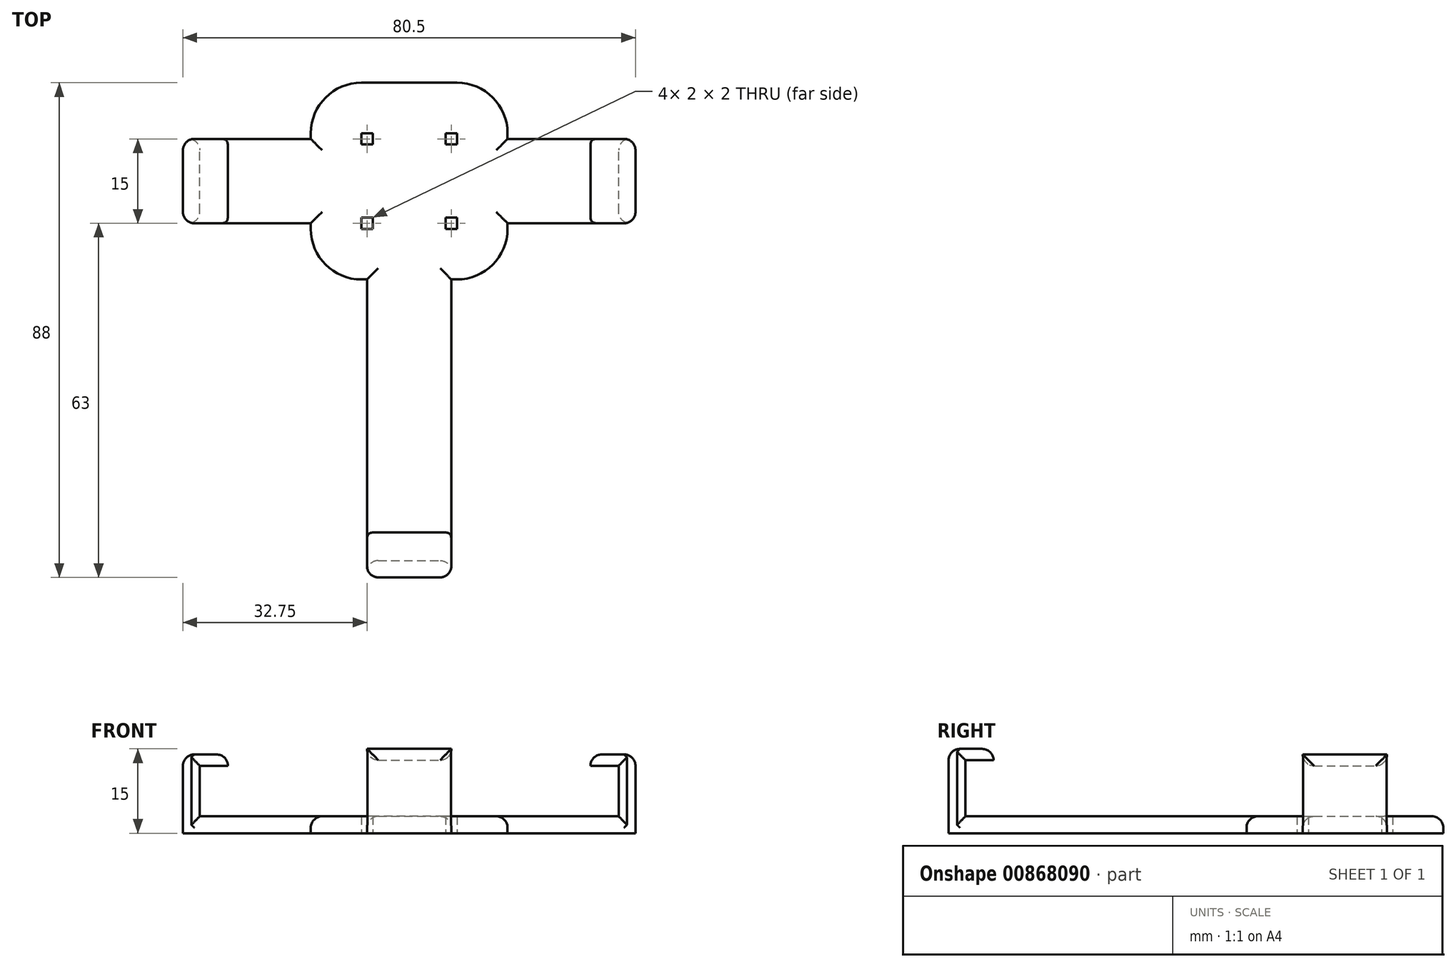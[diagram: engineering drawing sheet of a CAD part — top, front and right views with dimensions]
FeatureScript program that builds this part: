
annotation { "Feature Type Name" : "Feature", "Feature Type Description" : "" }
export const myFeature = defineFeature(function(context is Context, id is Id, definition is map)
    precondition{}
    {
        {
            var Q0;
            Q0=qCreatedBy(makeId("Top.planeOp"),FACE);
            var sketch = newSketch(context, id + "F0", { "sketchPlane" : qUnion([Q0])});
            skLineSegment(sketch, "E0.bottom", {"start": v(17.5, -17.5) * mm, "end": v(-17.5, -17.5) * mm});
            skLineSegment(sketch, "E0.top", {"start": v(17.5, 17.5) * mm, "end": v(-17.5, 17.5) * mm});
            skLineSegment(sketch, "E0.left", {"start": v(17.5, -17.5) * mm, "end": v(17.5, 17.5) * mm});
            skLineSegment(sketch, "E0.right", {"start": v(-17.5, -17.5) * mm, "end": v(-17.5, 17.5) * mm});
            skPoint(sketch, "E0.middle", {"position": v(0, 0) * mm});
            skLineSegment(sketch, "E1.bottom", {"start": v(37.25, -7.5) * mm, "end": v(-37.25, -7.5) * mm});
            skLineSegment(sketch, "E1.top", {"start": v(37.25, 7.5) * mm, "end": v(-37.25, 7.5) * mm});
            skLineSegment(sketch, "E1.left", {"start": v(37.25, -7.5) * mm, "end": v(37.25, 7.5) * mm});
            skLineSegment(sketch, "E1.right", {"start": v(-37.25, -7.5) * mm, "end": v(-37.25, 7.5) * mm});
            skLineSegment(sketch, "E2.bottom", {"start": v(-37.25, 7.5) * mm, "end": v(-40.25, 7.5) * mm});
            skLineSegment(sketch, "E2.top", {"start": v(-37.25, -7.5) * mm, "end": v(-40.25, -7.5) * mm});
            skLineSegment(sketch, "E2.left", {"start": v(-37.25, 7.5) * mm, "end": v(-37.25, -7.5) * mm});
            skLineSegment(sketch, "E2.right", {"start": v(-40.25, 7.5) * mm, "end": v(-40.25, -7.5) * mm});
            skLineSegment(sketch, "E3.bottom", {"start": v(37.25, 7.5) * mm, "end": v(40.25, 7.5) * mm});
            skLineSegment(sketch, "E3.top", {"start": v(37.25, -7.5) * mm, "end": v(40.25, -7.5) * mm});
            skLineSegment(sketch, "E3.left", {"start": v(37.25, 7.5) * mm, "end": v(37.25, -7.5) * mm});
            skLineSegment(sketch, "E3.right", {"start": v(40.25, 7.5) * mm, "end": v(40.25, -7.5) * mm});
            skLineSegment(sketch, "E4.bottom", {"start": v(-7.5, -7.5) * mm, "end": v(7.5, -7.5) * mm});
            skLineSegment(sketch, "E4.top", {"start": v(-7.5, -67.5) * mm, "end": v(7.5, -67.5) * mm});
            skLineSegment(sketch, "E4.left", {"start": v(-7.5, -7.5) * mm, "end": v(-7.5, -67.5) * mm});
            skLineSegment(sketch, "E4.right", {"start": v(7.5, -7.5) * mm, "end": v(7.5, -67.5) * mm});
            skLineSegment(sketch, "E5.top", {"start": v(-7.5, -70.5) * mm, "end": v(7.5, -70.5) * mm});
            skLineSegment(sketch, "E5.left", {"start": v(-7.5, -67.5) * mm, "end": v(-7.5, -70.5) * mm});
            skLineSegment(sketch, "E5.right", {"start": v(7.5, -67.5) * mm, "end": v(7.5, -70.5) * mm});
            skLineSegment(sketch, "E6", {"start": v(17.5, 17.5) * mm, "end": v(-17.5, -17.5) * mm, "construction": true});
            skLineSegment(sketch, "E7", {"start": v(-17.5, 17.5) * mm, "end": v(17.5, -17.5) * mm, "construction": true});
            skLineSegment(sketch, "E8", {"start": v(0, 17.5) * mm, "end": v(0, -17.5) * mm, "construction": true});
            skLineSegment(sketch, "E9", {"start": v(17.5, 0) * mm, "end": v(-17.5, 0) * mm, "construction": true});
            skLineSegment(sketch, "E10.bottom", {"start": v(6.5, 8.5) * mm, "end": v(8.5, 8.5) * mm});
            skLineSegment(sketch, "E10.top", {"start": v(6.5, 6.5) * mm, "end": v(8.5, 6.5) * mm});
            skLineSegment(sketch, "E10.left", {"start": v(6.5, 8.5) * mm, "end": v(6.5, 6.5) * mm});
            skLineSegment(sketch, "E10.right", {"start": v(8.5, 8.5) * mm, "end": v(8.5, 6.5) * mm});
            skPoint(sketch, "E10.middle", {"position": v(7.5, 7.5) * mm});
            skPoint(sketch, "E11.middle", {"position": v(-7.5, 7.5) * mm});
            skLineSegment(sketch, "E12.bottom", {"start": v(-8.5, -6.5) * mm, "end": v(-6.5, -6.5) * mm});
            skLineSegment(sketch, "E12.top", {"start": v(-8.5, -8.5) * mm, "end": v(-6.5, -8.5) * mm});
            skLineSegment(sketch, "E12.left", {"start": v(-8.5, -6.5) * mm, "end": v(-8.5, -8.5) * mm});
            skLineSegment(sketch, "E12.right", {"start": v(-6.5, -6.5) * mm, "end": v(-6.5, -8.5) * mm});
            skPoint(sketch, "E12.middle", {"position": v(-7.5, -7.5) * mm});
            skLineSegment(sketch, "E13.bottom", {"start": v(6.5, -6.5) * mm, "end": v(8.5, -6.5) * mm});
            skLineSegment(sketch, "E13.top", {"start": v(6.5, -8.5) * mm, "end": v(8.5, -8.5) * mm});
            skLineSegment(sketch, "E13.left", {"start": v(6.5, -6.5) * mm, "end": v(6.5, -8.5) * mm});
            skLineSegment(sketch, "E13.right", {"start": v(8.5, -6.5) * mm, "end": v(8.5, -8.5) * mm});
            skPoint(sketch, "E13.middle", {"position": v(7.5, -7.5) * mm});
            skLineSegment(sketch, "E14.MirrorCS", {"start": v(-6.5, 8.5) * mm, "end": v(-6.5, 6.5) * mm});
            skLineSegment(sketch, "E15.MirrorCS", {"start": v(-6.5, 8.5) * mm, "end": v(-8.5, 8.5) * mm});
            skLineSegment(sketch, "E16.MirrorCS", {"start": v(-8.5, 8.5) * mm, "end": v(-8.5, 6.5) * mm});
            skLineSegment(sketch, "E17.MirrorCS", {"start": v(-6.5, 6.5) * mm, "end": v(-8.5, 6.5) * mm});
            skSolve(sketch);
        }
        {
            var Q0;
            {var subQ1=sQuery(id+"F0.wireOp",EDGE,"E12.bottom");var subQ7=sQuery(id+"F0.wireOp",EDGE,"E13.bottom");Q0=qUnion([makeQuery(id+"F0.imprint","IMPRINT",FACE,{"disambiguationData":[TD([[makeQuery(id+"F0.imprint","IMPRINT",EDGE,{"derivedFrom":subQ7}),-1.0]])]}),makeQuery(id+"F0.imprint","IMPRINT",FACE,{"disambiguationData":[TD([[makeQuery(id+"F0.imprint","IMPRINT",EDGE,{"derivedFrom":subQ1}),-1.0]])]})]);}
            var Q1;
            {var subQ15=sQuery(id+"F0.wireOp",EDGE,"E0.top");Q1=makeQuery(id+"F0.imprint","IMPRINT",FACE,{"disambiguationData":[TD([[makeQuery(id+"F0.imprint","IMPRINT",EDGE,{"derivedFrom":subQ15}),1.0]])]});}
            var Q2;
            {var subQ5=sQuery(id+"F0.wireOp",EDGE,"E1.right");Q2=makeQuery(id+"F0.imprint","IMPRINT",FACE,{"disambiguationData":[TD([[makeQuery(id+"F0.imprint","IMPRINT",EDGE,{"derivedFrom":subQ5}),-1.0]])]});}
            var Q3;
            {var subQ1=sQuery(id+"F0.wireOp",EDGE,"E0.bottom");var subQ6=sQuery(id+"F0.wireOp",EDGE,"E0.right");var subQ10=makeQuery(id+"F0.imprint","INTERSECT",VERTEX,{"derivedFrom":[subQ1,subQ6]});Q3=makeQuery(id+"F0.imprint","IMPRINT",FACE,{"disambiguationData":[TD([[makeQuery(id+"F0.imprint","IMPRINT",EDGE,{"disambiguationData":[TD([[subQ10,1.0]])],"derivedFrom":subQ1}),-1.0]])]});}
            var Q4;
            {var subQ0=sQuery(id+"F0.wireOp",EDGE,"E4.left");var subQ1=sQuery(id+"F0.wireOp",EDGE,"E1.bottom");var subQ2=makeQuery(id+"F0.imprint","INTERSECT",VERTEX,{"derivedFrom":[subQ1,subQ0]});var subQ8=sQuery(id+"F0.wireOp",EDGE,"E13.left");var subQ9=makeQuery(id+"F0.imprint","INTERSECT",VERTEX,{"derivedFrom":[subQ1,subQ8]});Q4=qUnion([makeQuery(id+"F0.imprint","IMPRINT",FACE,{"disambiguationData":[TD([[makeQuery(id+"F0.imprint","IMPRINT",EDGE,{"disambiguationData":[TD([[subQ9,1.0]])],"derivedFrom":subQ1}),1.0]])]}),makeQuery(id+"F0.imprint","IMPRINT",FACE,{"disambiguationData":[TD([[makeQuery(id+"F0.imprint","IMPRINT",EDGE,{"disambiguationData":[TD([[subQ2,1.0]])],"derivedFrom":subQ1}),1.0]])]})]);}
            var Q5;
            {var subQ0=sQuery(id+"F0.wireOp",EDGE,"E4.right");var subQ1=sQuery(id+"F0.wireOp",EDGE,"E0.bottom");var subQ2=makeQuery(id+"F0.imprint","INTERSECT",VERTEX,{"derivedFrom":[subQ1,subQ0]});Q5=makeQuery(id+"F0.imprint","IMPRINT",FACE,{"disambiguationData":[TD([[makeQuery(id+"F0.imprint","IMPRINT",EDGE,{"disambiguationData":[TD([[subQ2,1.0]])],"derivedFrom":subQ1}),-1.0]])]});}
            var Q6;
            {var subQ5=sQuery(id+"F0.wireOp",EDGE,"E1.left");Q6=makeQuery(id+"F0.imprint","IMPRINT",FACE,{"disambiguationData":[TD([[makeQuery(id+"F0.imprint","IMPRINT",EDGE,{"derivedFrom":subQ5}),1.0]])]});}
            var Q7;
            {var subQ5=sQuery(id+"F0.wireOp",EDGE,"E4.top");Q7=makeQuery(id+"F0.imprint","IMPRINT",FACE,{"disambiguationData":[TD([[makeQuery(id+"F0.imprint","IMPRINT",EDGE,{"derivedFrom":subQ5}),1.0]])]});}
            var Q8;
            {var subQ5=sQuery(id+"F0.wireOp",EDGE,"E10.top");Q8=makeQuery(id+"F0.imprint","IMPRINT",FACE,{"disambiguationData":[TD([[makeQuery(id+"F0.imprint","IMPRINT",EDGE,{"derivedFrom":subQ5}),-1.0]])]});}
            var Q9;
            {var subQ0=sQuery(id+"F0.wireOp",EDGE,"E4.right");var subQ1=sQuery(id+"F0.wireOp",EDGE,"E0.bottom");var subQ2=makeQuery(id+"F0.imprint","INTERSECT",VERTEX,{"derivedFrom":[subQ1,subQ0]});Q9=makeQuery(id+"F0.imprint","IMPRINT",FACE,{"disambiguationData":[TD([[makeQuery(id+"F0.imprint","IMPRINT",EDGE,{"disambiguationData":[TD([[subQ2,-1.0]])],"derivedFrom":subQ1}),-1.0]])]});}
            extrude(context, id + "F1", {"entities" : qUnion([Q0, Q1, Q2, Q3, Q4, Q5, Q6, Q7, Q8, Q9]), "depth" : 3 * mm, "offsetDistance" : 25 * mm});
        }
        {
            var Q0;
            Q0=makeQuery(id+"F0.imprint","IMPRINT",FACE,{"disambiguationData":[TD([[makeQuery(id+"F0.imprint","IMPRINT",EDGE,{"derivedFrom":sQuery(id+"F0.wireOp",EDGE,"E1.right")}),1.0]])]});
            var Q1;
            Q1=makeQuery(id+"F0.imprint","IMPRINT",FACE,{"disambiguationData":[TD([[makeQuery(id+"F0.imprint","IMPRINT",EDGE,{"derivedFrom":sQuery(id+"F0.wireOp",EDGE,"E1.left")}),-1.0]])]});
            extrude(context, id + "F2", {"entities" : qUnion([Q0, Q1]), "operationType" : NewBodyOperationType.ADD, "depth" : 14 * mm, "offsetDistance" : 25 * mm});
        }
        {
            var Q0;
            Q0=makeQuery(id+"F0.imprint","IMPRINT",FACE,{"disambiguationData":[TD([[makeQuery(id+"F0.imprint","IMPRINT",EDGE,{"derivedFrom":sQuery(id+"F0.wireOp",EDGE,"E4.top")}),-1.0]])]});
            extrude(context, id + "F3", {"entities" : qUnion([Q0]), "operationType" : NewBodyOperationType.ADD, "depth" : 15 * mm, "offsetDistance" : 25 * mm});
        }
        {
            var Q0;
            Q0=makeQuery(id+"F3.opExtrude","SWEPT_FACE",FACE,{"disambiguationData":[OSD([sQuery(id+"F0.wireOp",EDGE,"E4.top")])]});
            var sketch = newSketch(context, id + "F4", { "sketchPlane" : qUnion([Q0])});
            skLineSegment(sketch, "E18.bottom", {"start": v(7.5, 15) * mm, "end": v(-7.5, 15) * mm});
            skLineSegment(sketch, "E18.top", {"start": v(7.5, 13) * mm, "end": v(-7.5, 13) * mm});
            skLineSegment(sketch, "E18.left", {"start": v(7.5, 15) * mm, "end": v(7.5, 13) * mm});
            skLineSegment(sketch, "E18.right", {"start": v(-7.5, 15) * mm, "end": v(-7.5, 13) * mm});
            skSolve(sketch);
        }
        {
            var Q0;
            Q0 = qSketchRegion(id + "F4", true);
            extrude(context, id + "F5", {"entities" : qUnion([Q0]), "operationType" : NewBodyOperationType.ADD, "depth" : 5 * mm, "offsetDistance" : 25 * mm});
        }
        {
            var Q0;
            Q0=makeQuery(id+"F2.opExtrude","SWEPT_FACE",FACE,{"disambiguationData":[OSD([sQuery(id+"F0.wireOp",EDGE,"E1.right")])]});
            var sketch = newSketch(context, id + "F6", { "sketchPlane" : qUnion([Q0])});
            skLineSegment(sketch, "E19.bottom", {"start": v(7.5, 14) * mm, "end": v(-7.5, 14) * mm});
            skLineSegment(sketch, "E19.top", {"start": v(7.5, 12) * mm, "end": v(-7.5, 12) * mm});
            skLineSegment(sketch, "E19.left", {"start": v(7.5, 14) * mm, "end": v(7.5, 12) * mm});
            skLineSegment(sketch, "E19.right", {"start": v(-7.5, 14) * mm, "end": v(-7.5, 12) * mm});
            skSolve(sketch);
        }
        {
            var Q0;
            Q0 = qSketchRegion(id + "F6", true);
            extrude(context, id + "F7", {"entities" : qUnion([Q0]), "operationType" : NewBodyOperationType.ADD, "depth" : 5 * mm, "offsetDistance" : 25 * mm});
        }
        {
            var Q0;
            Q0=makeQuery(id+"F2.opExtrude","SWEPT_FACE",FACE,{"disambiguationData":[OSD([sQuery(id+"F0.wireOp",EDGE,"E1.left")])]});
            var sketch = newSketch(context, id + "F8", { "sketchPlane" : qUnion([Q0])});
            skLineSegment(sketch, "E20.bottom", {"start": v(7.5, 14) * mm, "end": v(-7.5, 14) * mm});
            skLineSegment(sketch, "E20.top", {"start": v(7.5, 12) * mm, "end": v(-7.5, 12) * mm});
            skLineSegment(sketch, "E20.left", {"start": v(7.5, 14) * mm, "end": v(7.5, 12) * mm});
            skLineSegment(sketch, "E20.right", {"start": v(-7.5, 14) * mm, "end": v(-7.5, 12) * mm});
            skSolve(sketch);
        }
        {
            var Q0;
            Q0 = qSketchRegion(id + "F8", true);
            extrude(context, id + "F9", {"entities" : qUnion([Q0]), "operationType" : NewBodyOperationType.ADD, "depth" : 5 * mm, "offsetDistance" : 25 * mm});
        }
        {
            var Q0;
            {var subQ0=sQuery(id+"F0.wireOp",EDGE,"E13.left");var subQ1=sQuery(id+"F0.wireOp",EDGE,"E1.bottom");var subQ2=makeQuery(id+"F0.imprint","INTERSECT",VERTEX,{"derivedFrom":[subQ1,subQ0]});Q0=makeQuery(id+"F0.imprint","IMPRINT",FACE,{"disambiguationData":[TD([[makeQuery(id+"F0.imprint","IMPRINT",EDGE,{"disambiguationData":[TD([[subQ2,1.0]])],"derivedFrom":subQ1}),1.0]])]});}
            var Q1;
            {var subQ0=sQuery(id+"F0.wireOp",EDGE,"E4.right");var subQ1=sQuery(id+"F0.wireOp",EDGE,"E1.bottom");var subQ2=makeQuery(id+"F0.imprint","INTERSECT",VERTEX,{"derivedFrom":[subQ1,subQ0]});Q1=makeQuery(id+"F0.imprint","IMPRINT",FACE,{"disambiguationData":[TD([[makeQuery(id+"F0.imprint","IMPRINT",EDGE,{"disambiguationData":[TD([[subQ2,1.0]])],"derivedFrom":subQ1}),1.0]])]});}
            var Q2;
            {var subQ0=sQuery(id+"F0.wireOp",EDGE,"E13.bottom");Q2=makeQuery(id+"F0.imprint","IMPRINT",FACE,{"disambiguationData":[TD([[makeQuery(id+"F0.imprint","IMPRINT",EDGE,{"derivedFrom":subQ0}),-1.0]])]});}
            var Q3;
            {var subQ5=sQuery(id+"F0.wireOp",EDGE,"E10.bottom");Q3=makeQuery(id+"F0.imprint","IMPRINT",FACE,{"disambiguationData":[TD([[makeQuery(id+"F0.imprint","IMPRINT",EDGE,{"derivedFrom":subQ5}),-1.0]])]});}
            var Q4;
            {var subQ5=sQuery(id+"F0.wireOp",EDGE,"E10.top");Q4=makeQuery(id+"F0.imprint","IMPRINT",FACE,{"disambiguationData":[TD([[makeQuery(id+"F0.imprint","IMPRINT",EDGE,{"derivedFrom":subQ5}),1.0]])]});}
            var Q5;
            {var subQ5=sQuery(id+"F0.wireOp",EDGE,"E17.MirrorCS");Q5=makeQuery(id+"F0.imprint","IMPRINT",FACE,{"disambiguationData":[TD([[makeQuery(id+"F0.imprint","IMPRINT",EDGE,{"derivedFrom":subQ5}),-1.0]])]});}
            var Q6;
            {var subQ5=sQuery(id+"F0.wireOp",EDGE,"E15.MirrorCS");Q6=makeQuery(id+"F0.imprint","IMPRINT",FACE,{"disambiguationData":[TD([[makeQuery(id+"F0.imprint","IMPRINT",EDGE,{"derivedFrom":subQ5}),1.0]])]});}
            var Q7;
            {var subQ1=sQuery(id+"F0.wireOp",EDGE,"E12.bottom");Q7=makeQuery(id+"F0.imprint","IMPRINT",FACE,{"disambiguationData":[TD([[makeQuery(id+"F0.imprint","IMPRINT",EDGE,{"derivedFrom":subQ1}),-1.0]])]});}
            var Q8;
            {var subQ0=sQuery(id+"F0.wireOp",EDGE,"E4.left");var subQ1=sQuery(id+"F0.wireOp",EDGE,"E1.bottom");var subQ2=makeQuery(id+"F0.imprint","INTERSECT",VERTEX,{"derivedFrom":[subQ1,subQ0]});Q8=makeQuery(id+"F0.imprint","IMPRINT",FACE,{"disambiguationData":[TD([[makeQuery(id+"F0.imprint","IMPRINT",EDGE,{"disambiguationData":[TD([[subQ2,-1.0]])],"derivedFrom":subQ1}),1.0]])]});}
            var Q9;
            {var subQ0=sQuery(id+"F0.wireOp",EDGE,"E4.left");var subQ1=sQuery(id+"F0.wireOp",EDGE,"E1.bottom");var subQ2=makeQuery(id+"F0.imprint","INTERSECT",VERTEX,{"derivedFrom":[subQ1,subQ0]});Q9=makeQuery(id+"F0.imprint","IMPRINT",FACE,{"disambiguationData":[TD([[makeQuery(id+"F0.imprint","IMPRINT",EDGE,{"disambiguationData":[TD([[subQ2,1.0]])],"derivedFrom":subQ1}),1.0]])]});}
            extrude(context, id + "F10", {"entities" : qUnion([Q0, Q1, Q2, Q3, Q4, Q5, Q6, Q7, Q8, Q9]), "operationType" : NewBodyOperationType.REMOVE, "depth" : 25 * mm, "offsetDistance" : 25 * mm});
        }
        {
            var Q0;
            Q0=makeQuery(id+"F2.opExtrude","CAP_EDGE",EDGE,{"disambiguationData":[OSD([sQuery(id+"F0.wireOp",EDGE,"E2.right")])],"isStart":false});
            var Q1;
            Q1=makeQuery(id+"F2.opExtrude","CAP_EDGE",EDGE,{"disambiguationData":[OSD([sQuery(id+"F0.wireOp",EDGE,"E3.right")])],"isStart":false});
            var Q2;
            Q2=makeQuery(id+"F3.opExtrude","CAP_EDGE",EDGE,{"disambiguationData":[OSD([sQuery(id+"F0.wireOp",EDGE,"E5.top")])],"isStart":false});
            var Q3;
            Q3=makeQuery(id+"F2.opExtrude","SWEPT_EDGE",EDGE,{"disambiguationData":[OSD([sQuery(id+"F0.wireOp",EDGE,"E2.top"),sQuery(id+"F0.wireOp",EDGE,"E2.right")])]});
            var Q4;
            Q4=makeQuery(id+"F2.opExtrude","SWEPT_EDGE",EDGE,{"disambiguationData":[OSD([sQuery(id+"F0.wireOp",EDGE,"E2.bottom"),sQuery(id+"F0.wireOp",EDGE,"E2.right")])]});
            var Q5;
            Q5=makeQuery(id+"F2.opExtrude","SWEPT_EDGE",EDGE,{"disambiguationData":[OSD([sQuery(id+"F0.wireOp",EDGE,"E3.top"),sQuery(id+"F0.wireOp",EDGE,"E3.right")])]});
            var Q6;
            Q6=makeQuery(id+"F2.opExtrude","SWEPT_EDGE",EDGE,{"disambiguationData":[OSD([sQuery(id+"F0.wireOp",EDGE,"E3.bottom"),sQuery(id+"F0.wireOp",EDGE,"E3.right")])]});
            var Q7;
            Q7=makeQuery(id+"F3.opExtrude","SWEPT_EDGE",EDGE,{"disambiguationData":[OSD([sQuery(id+"F0.wireOp",EDGE,"E5.top"),sQuery(id+"F0.wireOp",EDGE,"E5.left")])]});
            var Q8;
            Q8=makeQuery(id+"F3.opExtrude","SWEPT_EDGE",EDGE,{"disambiguationData":[OSD([sQuery(id+"F0.wireOp",EDGE,"E5.top"),sQuery(id+"F0.wireOp",EDGE,"E5.right")])]});
            var Q9;
            Q9=makeQuery(id+"F9.opExtrude","CAP_EDGE",EDGE,{"disambiguationData":[OSD([sQuery(id+"F8.wireOp",EDGE,"E20.bottom")])],"isStart":false});
            var Q10;
            Q10=makeQuery(id+"F7.opExtrude","CAP_EDGE",EDGE,{"disambiguationData":[OSD([sQuery(id+"F6.wireOp",EDGE,"E19.bottom")])],"isStart":false});
            var Q11;
            Q11=makeQuery(id+"F5.opExtrude","CAP_EDGE",EDGE,{"disambiguationData":[OSD([sQuery(id+"F4.wireOp",EDGE,"E18.bottom")])],"isStart":false});
            var Q12;
            {var subQ0=sQuery(id+"F0.wireOp",EDGE,"E4.left");Q12=makeQuery(id+"F1.opExtrude","CAP_EDGE",EDGE,{"disambiguationData":[OSD([subQ0]),TDD([makeQuery(id+"F0.imprint","IMPRINT",EDGE,{"disambiguationData":[TD([[makeQuery(id+"F0.imprint","INTERSECT",VERTEX,{"derivedFrom":[sQuery(id+"F0.wireOp",EDGE,"E0.bottom"),subQ0]}),-1.0]])],"derivedFrom":subQ0})])],"isStart":false});}
            var Q13;
            {var subQ0=sQuery(id+"F0.wireOp",EDGE,"E4.right");Q13=makeQuery(id+"F1.opExtrude","CAP_EDGE",EDGE,{"disambiguationData":[OSD([subQ0]),TDD([makeQuery(id+"F0.imprint","IMPRINT",EDGE,{"disambiguationData":[TD([[makeQuery(id+"F0.imprint","INTERSECT",VERTEX,{"derivedFrom":[sQuery(id+"F0.wireOp",EDGE,"E0.bottom"),subQ0]}),-1.0]])],"derivedFrom":subQ0})])],"isStart":false});}
            var Q14;
            {var subQ0=sQuery(id+"F0.wireOp",EDGE,"E0.bottom");Q14=makeQuery(id+"F1.opExtrude","CAP_EDGE",EDGE,{"disambiguationData":[OSD([subQ0]),TDD([makeQuery(id+"F0.imprint","IMPRINT",EDGE,{"disambiguationData":[TD([[makeQuery(id+"F0.imprint","INTERSECT",VERTEX,{"derivedFrom":[subQ0,sQuery(id+"F0.wireOp",EDGE,"E4.right")]}),1.0]])],"derivedFrom":subQ0})])],"isStart":false});}
            var Q15;
            {var subQ0=sQuery(id+"F0.wireOp",EDGE,"E0.bottom");Q15=makeQuery(id+"F1.opExtrude","CAP_EDGE",EDGE,{"disambiguationData":[OSD([subQ0]),TDD([makeQuery(id+"F0.imprint","IMPRINT",EDGE,{"disambiguationData":[TD([[makeQuery(id+"F0.imprint","INTERSECT",VERTEX,{"derivedFrom":[subQ0,sQuery(id+"F0.wireOp",EDGE,"E0.right")]}),1.0]])],"derivedFrom":subQ0})])],"isStart":false});}
            var Q16;
            {var subQ0=sQuery(id+"F0.wireOp",EDGE,"E0.right");Q16=makeQuery(id+"F1.opExtrude","CAP_EDGE",EDGE,{"disambiguationData":[OSD([subQ0]),TDD([makeQuery(id+"F0.imprint","IMPRINT",EDGE,{"disambiguationData":[TD([[makeQuery(id+"F0.imprint","INTERSECT",VERTEX,{"derivedFrom":[sQuery(id+"F0.wireOp",EDGE,"E0.bottom"),subQ0]}),-1.0]])],"derivedFrom":subQ0})])],"isStart":false});}
            var Q17;
            {var subQ0=sQuery(id+"F0.wireOp",EDGE,"E0.right");Q17=makeQuery(id+"F1.opExtrude","CAP_EDGE",EDGE,{"disambiguationData":[OSD([subQ0]),TDD([makeQuery(id+"F0.imprint","IMPRINT",EDGE,{"disambiguationData":[TD([[makeQuery(id+"F0.imprint","INTERSECT",VERTEX,{"derivedFrom":[sQuery(id+"F0.wireOp",EDGE,"E0.top"),subQ0]}),1.0]])],"derivedFrom":subQ0})])],"isStart":false});}
            var Q18;
            Q18=makeQuery(id+"F1.opExtrude","CAP_EDGE",EDGE,{"disambiguationData":[OSD([sQuery(id+"F0.wireOp",EDGE,"E0.top")])],"isStart":false});
            var Q19;
            {var subQ0=sQuery(id+"F0.wireOp",EDGE,"E0.left");Q19=makeQuery(id+"F1.opExtrude","CAP_EDGE",EDGE,{"disambiguationData":[OSD([subQ0]),TDD([makeQuery(id+"F0.imprint","IMPRINT",EDGE,{"disambiguationData":[TD([[makeQuery(id+"F0.imprint","INTERSECT",VERTEX,{"derivedFrom":[sQuery(id+"F0.wireOp",EDGE,"E0.top"),subQ0]}),1.0]])],"derivedFrom":subQ0})])],"isStart":false});}
            var Q20;
            {var subQ0=sQuery(id+"F0.wireOp",EDGE,"E0.left");Q20=makeQuery(id+"F1.opExtrude","CAP_EDGE",EDGE,{"disambiguationData":[OSD([subQ0]),TDD([makeQuery(id+"F0.imprint","IMPRINT",EDGE,{"disambiguationData":[TD([[makeQuery(id+"F0.imprint","INTERSECT",VERTEX,{"derivedFrom":[subQ0,sQuery(id+"F0.wireOp",EDGE,"E1.bottom")]}),1.0]])],"derivedFrom":subQ0})])],"isStart":false});}
            var Q21;
            {var subQ0=sQuery(id+"F0.wireOp",EDGE,"E1.bottom");Q21=makeQuery(id+"F1.opExtrude","CAP_EDGE",EDGE,{"disambiguationData":[OSD([subQ0]),TDD([makeQuery(id+"F0.imprint","IMPRINT",EDGE,{"disambiguationData":[TD([[makeQuery(id+"F0.imprint","INTERSECT",VERTEX,{"derivedFrom":[sQuery(id+"F0.wireOp",EDGE,"E0.right"),subQ0]}),-1.0]])],"derivedFrom":subQ0})])],"isStart":false});}
            var Q22;
            {var subQ0=sQuery(id+"F0.wireOp",EDGE,"E1.top");Q22=makeQuery(id+"F1.opExtrude","CAP_EDGE",EDGE,{"disambiguationData":[OSD([subQ0]),TDD([makeQuery(id+"F0.imprint","IMPRINT",EDGE,{"disambiguationData":[TD([[makeQuery(id+"F0.imprint","INTERSECT",VERTEX,{"derivedFrom":[sQuery(id+"F0.wireOp",EDGE,"E0.right"),subQ0]}),-1.0]])],"derivedFrom":subQ0})])],"isStart":false});}
            var Q23;
            {var subQ0=sQuery(id+"F0.wireOp",EDGE,"E1.top");Q23=makeQuery(id+"F1.opExtrude","CAP_EDGE",EDGE,{"disambiguationData":[OSD([subQ0]),TDD([makeQuery(id+"F0.imprint","IMPRINT",EDGE,{"disambiguationData":[TD([[makeQuery(id+"F0.imprint","INTERSECT",VERTEX,{"derivedFrom":[sQuery(id+"F0.wireOp",EDGE,"E0.left"),subQ0]}),1.0]])],"derivedFrom":subQ0})])],"isStart":false});}
            var Q24;
            {var subQ0=sQuery(id+"F0.wireOp",EDGE,"E1.bottom");Q24=makeQuery(id+"F1.opExtrude","CAP_EDGE",EDGE,{"disambiguationData":[OSD([subQ0]),TDD([makeQuery(id+"F0.imprint","IMPRINT",EDGE,{"disambiguationData":[TD([[makeQuery(id+"F0.imprint","INTERSECT",VERTEX,{"derivedFrom":[sQuery(id+"F0.wireOp",EDGE,"E0.left"),subQ0]}),1.0]])],"derivedFrom":subQ0})])],"isStart":false});}
            fillet(context, id + "F11", {"entities" : qUnion([Q0, Q1, Q2, Q3, Q4, Q5, Q6, Q7, Q8, Q9, Q10, Q11, Q12, Q13, Q14, Q15, Q16, Q17, Q18, Q19, Q20, Q21, Q22, Q23, Q24]), "radius" : 2 * mm, "tangentPropagation" : true, "allowEdgeOverflow" : false});
        }
        {
            var Q0;
            {var subQ0=sQuery(id+"F0.wireOp",EDGE,"E3.bottom");var subQ1=sQuery(id+"F0.wireOp",EDGE,"E1.top");Q0=makeQuery(id+"FFY5rLaEK2HNcOl_1.opChamfer","BLEND_EDGE",EDGE,{"blendedFrom":[makeQuery(id+"F9.opExtrude","CAP_EDGE",EDGE,{"disambiguationData":[OSD([sQuery(id+"F8.wireOp",EDGE,"E20.top")])],"isStart":false}),makeQuery(id+"F9.boolean.opBoolean","MERGE",FACE,{"derivedFrom":[makeQuery(id+"F2.boolean.opBoolean","MERGE",FACE,{"derivedFrom":[makeQuery(id+"F1.opExtrude","SWEPT_FACE",FACE,{"disambiguationData":[OSD([subQ1]),TDD([makeQuery(id+"F0.imprint","IMPRINT",EDGE,{"disambiguationData":[TD([[makeQuery(id+"F0.imprint","INTERSECT",VERTEX,{"derivedFrom":[sQuery(id+"F0.wireOp",EDGE,"E0.left"),subQ1]}),1.0]])],"derivedFrom":subQ1})])]}),makeQuery(id+"F2.opExtrude","SWEPT_FACE",FACE,{"disambiguationData":[OSD([subQ0])]})]}),makeQuery(id+"F9.opExtrude","SWEPT_FACE",FACE,{"disambiguationData":[OSD([sQuery(id+"F8.wireOp",EDGE,"E20.right")])]})]})],"blendedInto":[makeQuery(id+"F9.boolean.opBoolean","MERGE",FACE,{"derivedFrom":[makeQuery(id+"F2.boolean.opBoolean","MERGE",FACE,{"derivedFrom":[makeQuery(id+"F1.opExtrude","SWEPT_FACE",FACE,{"disambiguationData":[OSD([subQ1]),TDD([makeQuery(id+"F0.imprint","IMPRINT",EDGE,{"disambiguationData":[TD([[makeQuery(id+"F0.imprint","INTERSECT",VERTEX,{"derivedFrom":[sQuery(id+"F0.wireOp",EDGE,"E0.left"),subQ1]}),1.0]])],"derivedFrom":subQ1})])]}),makeQuery(id+"F2.opExtrude","SWEPT_FACE",FACE,{"disambiguationData":[OSD([subQ0])]})]}),makeQuery(id+"F9.opExtrude","SWEPT_FACE",FACE,{"disambiguationData":[OSD([sQuery(id+"F8.wireOp",EDGE,"E20.right")])]})]})]});}
            var Q1;
            Q1=makeQuery(id+"F2.opExtrude","SWEPT_EDGE",EDGE,{"disambiguationData":[OSD([sQuery(id+"F0.wireOp",EDGE,"E1.top"),sQuery(id+"F0.wireOp",EDGE,"E1.left"),sQuery(id+"F0.wireOp",EDGE,"E3.bottom")])]});
            var Q2;
            Q2=makeQuery(id+"F2.opExtrude","SWEPT_EDGE",EDGE,{"disambiguationData":[OSD([sQuery(id+"F0.wireOp",EDGE,"E1.bottom"),sQuery(id+"F0.wireOp",EDGE,"E1.left"),sQuery(id+"F0.wireOp",EDGE,"E3.top")])]});
            var Q3;
            {var subQ0=sQuery(id+"F0.wireOp",EDGE,"E3.top");var subQ1=sQuery(id+"F0.wireOp",EDGE,"E1.bottom");Q3=makeQuery(id+"FFY5rLaEK2HNcOl_1.opChamfer","BLEND_EDGE",EDGE,{"blendedFrom":[makeQuery(id+"F9.opExtrude","CAP_EDGE",EDGE,{"disambiguationData":[OSD([sQuery(id+"F8.wireOp",EDGE,"E20.top")])],"isStart":false}),makeQuery(id+"F9.boolean.opBoolean","MERGE",FACE,{"derivedFrom":[makeQuery(id+"F2.boolean.opBoolean","MERGE",FACE,{"derivedFrom":[makeQuery(id+"F1.opExtrude","SWEPT_FACE",FACE,{"disambiguationData":[OSD([subQ1]),TDD([makeQuery(id+"F0.imprint","IMPRINT",EDGE,{"disambiguationData":[TD([[makeQuery(id+"F0.imprint","INTERSECT",VERTEX,{"derivedFrom":[sQuery(id+"F0.wireOp",EDGE,"E0.left"),subQ1]}),1.0]])],"derivedFrom":subQ1})])]}),makeQuery(id+"F2.opExtrude","SWEPT_FACE",FACE,{"disambiguationData":[OSD([subQ0])]})]}),makeQuery(id+"F9.opExtrude","SWEPT_FACE",FACE,{"disambiguationData":[OSD([sQuery(id+"F8.wireOp",EDGE,"E20.left")])]})]})],"blendedInto":[makeQuery(id+"F9.boolean.opBoolean","MERGE",FACE,{"derivedFrom":[makeQuery(id+"F2.boolean.opBoolean","MERGE",FACE,{"derivedFrom":[makeQuery(id+"F1.opExtrude","SWEPT_FACE",FACE,{"disambiguationData":[OSD([subQ1]),TDD([makeQuery(id+"F0.imprint","IMPRINT",EDGE,{"disambiguationData":[TD([[makeQuery(id+"F0.imprint","INTERSECT",VERTEX,{"derivedFrom":[sQuery(id+"F0.wireOp",EDGE,"E0.left"),subQ1]}),1.0]])],"derivedFrom":subQ1})])]}),makeQuery(id+"F2.opExtrude","SWEPT_FACE",FACE,{"disambiguationData":[OSD([subQ0])]})]}),makeQuery(id+"F9.opExtrude","SWEPT_FACE",FACE,{"disambiguationData":[OSD([sQuery(id+"F8.wireOp",EDGE,"E20.left")])]})]})]});}
            var Q4;
            Q4=makeQuery(id+"F2.opExtrude","SWEPT_EDGE",EDGE,{"disambiguationData":[OSD([sQuery(id+"F0.wireOp",EDGE,"E1.top"),sQuery(id+"F0.wireOp",EDGE,"E1.right"),sQuery(id+"F0.wireOp",EDGE,"E2.bottom")])]});
            var Q5;
            {var subQ0=sQuery(id+"F0.wireOp",EDGE,"E2.bottom");var subQ1=sQuery(id+"F0.wireOp",EDGE,"E1.top");Q5=makeQuery(id+"FFY5rLaEK2HNcOl_1.opChamfer","BLEND_EDGE",EDGE,{"blendedFrom":[makeQuery(id+"F7.opExtrude","CAP_EDGE",EDGE,{"disambiguationData":[OSD([sQuery(id+"F6.wireOp",EDGE,"E19.top")])],"isStart":false}),makeQuery(id+"F7.boolean.opBoolean","MERGE",FACE,{"derivedFrom":[makeQuery(id+"F2.boolean.opBoolean","MERGE",FACE,{"derivedFrom":[makeQuery(id+"F1.opExtrude","SWEPT_FACE",FACE,{"disambiguationData":[OSD([subQ1]),TDD([makeQuery(id+"F0.imprint","IMPRINT",EDGE,{"disambiguationData":[TD([[makeQuery(id+"F0.imprint","INTERSECT",VERTEX,{"derivedFrom":[sQuery(id+"F0.wireOp",EDGE,"E0.right"),subQ1]}),-1.0]])],"derivedFrom":subQ1})])]}),makeQuery(id+"F2.opExtrude","SWEPT_FACE",FACE,{"disambiguationData":[OSD([subQ0])]})]}),makeQuery(id+"F7.opExtrude","SWEPT_FACE",FACE,{"disambiguationData":[OSD([sQuery(id+"F6.wireOp",EDGE,"E19.left")])]})]})],"blendedInto":[makeQuery(id+"F7.boolean.opBoolean","MERGE",FACE,{"derivedFrom":[makeQuery(id+"F2.boolean.opBoolean","MERGE",FACE,{"derivedFrom":[makeQuery(id+"F1.opExtrude","SWEPT_FACE",FACE,{"disambiguationData":[OSD([subQ1]),TDD([makeQuery(id+"F0.imprint","IMPRINT",EDGE,{"disambiguationData":[TD([[makeQuery(id+"F0.imprint","INTERSECT",VERTEX,{"derivedFrom":[sQuery(id+"F0.wireOp",EDGE,"E0.right"),subQ1]}),-1.0]])],"derivedFrom":subQ1})])]}),makeQuery(id+"F2.opExtrude","SWEPT_FACE",FACE,{"disambiguationData":[OSD([subQ0])]})]}),makeQuery(id+"F7.opExtrude","SWEPT_FACE",FACE,{"disambiguationData":[OSD([sQuery(id+"F6.wireOp",EDGE,"E19.left")])]})]})]});}
            var Q6;
            {var subQ0=sQuery(id+"F0.wireOp",EDGE,"E2.top");var subQ1=sQuery(id+"F0.wireOp",EDGE,"E1.bottom");Q6=makeQuery(id+"FFY5rLaEK2HNcOl_1.opChamfer","BLEND_EDGE",EDGE,{"blendedFrom":[makeQuery(id+"F7.opExtrude","CAP_EDGE",EDGE,{"disambiguationData":[OSD([sQuery(id+"F6.wireOp",EDGE,"E19.top")])],"isStart":false}),makeQuery(id+"F7.boolean.opBoolean","MERGE",FACE,{"derivedFrom":[makeQuery(id+"F2.boolean.opBoolean","MERGE",FACE,{"derivedFrom":[makeQuery(id+"F1.opExtrude","SWEPT_FACE",FACE,{"disambiguationData":[OSD([subQ1]),TDD([makeQuery(id+"F0.imprint","IMPRINT",EDGE,{"disambiguationData":[TD([[makeQuery(id+"F0.imprint","INTERSECT",VERTEX,{"derivedFrom":[sQuery(id+"F0.wireOp",EDGE,"E0.right"),subQ1]}),-1.0]])],"derivedFrom":subQ1})])]}),makeQuery(id+"F2.opExtrude","SWEPT_FACE",FACE,{"disambiguationData":[OSD([subQ0])]})]}),makeQuery(id+"F7.opExtrude","SWEPT_FACE",FACE,{"disambiguationData":[OSD([sQuery(id+"F6.wireOp",EDGE,"E19.right")])]})]})],"blendedInto":[makeQuery(id+"F7.boolean.opBoolean","MERGE",FACE,{"derivedFrom":[makeQuery(id+"F2.boolean.opBoolean","MERGE",FACE,{"derivedFrom":[makeQuery(id+"F1.opExtrude","SWEPT_FACE",FACE,{"disambiguationData":[OSD([subQ1]),TDD([makeQuery(id+"F0.imprint","IMPRINT",EDGE,{"disambiguationData":[TD([[makeQuery(id+"F0.imprint","INTERSECT",VERTEX,{"derivedFrom":[sQuery(id+"F0.wireOp",EDGE,"E0.right"),subQ1]}),-1.0]])],"derivedFrom":subQ1})])]}),makeQuery(id+"F2.opExtrude","SWEPT_FACE",FACE,{"disambiguationData":[OSD([subQ0])]})]}),makeQuery(id+"F7.opExtrude","SWEPT_FACE",FACE,{"disambiguationData":[OSD([sQuery(id+"F6.wireOp",EDGE,"E19.right")])]})]})]});}
            var Q7;
            Q7=makeQuery(id+"F2.opExtrude","SWEPT_EDGE",EDGE,{"disambiguationData":[OSD([sQuery(id+"F0.wireOp",EDGE,"E1.bottom"),sQuery(id+"F0.wireOp",EDGE,"E1.right"),sQuery(id+"F0.wireOp",EDGE,"E2.top")])]});
            var Q8;
            Q8=makeQuery(id+"F3.opExtrude","SWEPT_EDGE",EDGE,{"disambiguationData":[OSD([sQuery(id+"F0.wireOp",EDGE,"E4.top"),sQuery(id+"F0.wireOp",EDGE,"E4.left"),sQuery(id+"F0.wireOp",EDGE,"E5.left")])]});
            var Q9;
            {var subQ0=sQuery(id+"F0.wireOp",EDGE,"E5.left");var subQ1=sQuery(id+"F0.wireOp",EDGE,"E4.left");Q9=makeQuery(id+"FFY5rLaEK2HNcOl_1.opChamfer","BLEND_EDGE",EDGE,{"blendedFrom":[makeQuery(id+"F5.opExtrude","CAP_EDGE",EDGE,{"disambiguationData":[OSD([sQuery(id+"F4.wireOp",EDGE,"E18.top")])],"isStart":false}),makeQuery(id+"F5.boolean.opBoolean","MERGE",FACE,{"derivedFrom":[makeQuery(id+"F3.boolean.opBoolean","MERGE",FACE,{"derivedFrom":[makeQuery(id+"F1.opExtrude","SWEPT_FACE",FACE,{"disambiguationData":[OSD([subQ1]),TDD([makeQuery(id+"F0.imprint","IMPRINT",EDGE,{"disambiguationData":[TD([[makeQuery(id+"F0.imprint","INTERSECT",VERTEX,{"derivedFrom":[sQuery(id+"F0.wireOp",EDGE,"E0.bottom"),subQ1]}),-1.0]])],"derivedFrom":subQ1})])]}),makeQuery(id+"F3.opExtrude","SWEPT_FACE",FACE,{"disambiguationData":[OSD([subQ0])]})]}),makeQuery(id+"F5.opExtrude","SWEPT_FACE",FACE,{"disambiguationData":[OSD([sQuery(id+"F4.wireOp",EDGE,"E18.left")])]})]})],"blendedInto":[makeQuery(id+"F5.boolean.opBoolean","MERGE",FACE,{"derivedFrom":[makeQuery(id+"F3.boolean.opBoolean","MERGE",FACE,{"derivedFrom":[makeQuery(id+"F1.opExtrude","SWEPT_FACE",FACE,{"disambiguationData":[OSD([subQ1]),TDD([makeQuery(id+"F0.imprint","IMPRINT",EDGE,{"disambiguationData":[TD([[makeQuery(id+"F0.imprint","INTERSECT",VERTEX,{"derivedFrom":[sQuery(id+"F0.wireOp",EDGE,"E0.bottom"),subQ1]}),-1.0]])],"derivedFrom":subQ1})])]}),makeQuery(id+"F3.opExtrude","SWEPT_FACE",FACE,{"disambiguationData":[OSD([subQ0])]})]}),makeQuery(id+"F5.opExtrude","SWEPT_FACE",FACE,{"disambiguationData":[OSD([sQuery(id+"F4.wireOp",EDGE,"E18.left")])]})]})]});}
            var Q10;
            {var subQ0=sQuery(id+"F0.wireOp",EDGE,"E5.right");var subQ1=sQuery(id+"F0.wireOp",EDGE,"E4.right");Q10=makeQuery(id+"FFY5rLaEK2HNcOl_1.opChamfer","BLEND_EDGE",EDGE,{"blendedFrom":[makeQuery(id+"F5.opExtrude","CAP_EDGE",EDGE,{"disambiguationData":[OSD([sQuery(id+"F4.wireOp",EDGE,"E18.top")])],"isStart":false}),makeQuery(id+"F5.boolean.opBoolean","MERGE",FACE,{"derivedFrom":[makeQuery(id+"F3.boolean.opBoolean","MERGE",FACE,{"derivedFrom":[makeQuery(id+"F1.opExtrude","SWEPT_FACE",FACE,{"disambiguationData":[OSD([subQ1]),TDD([makeQuery(id+"F0.imprint","IMPRINT",EDGE,{"disambiguationData":[TD([[makeQuery(id+"F0.imprint","INTERSECT",VERTEX,{"derivedFrom":[sQuery(id+"F0.wireOp",EDGE,"E0.bottom"),subQ1]}),-1.0]])],"derivedFrom":subQ1})])]}),makeQuery(id+"F3.opExtrude","SWEPT_FACE",FACE,{"disambiguationData":[OSD([subQ0])]})]}),makeQuery(id+"F5.opExtrude","SWEPT_FACE",FACE,{"disambiguationData":[OSD([sQuery(id+"F4.wireOp",EDGE,"E18.right")])]})]})],"blendedInto":[makeQuery(id+"F5.boolean.opBoolean","MERGE",FACE,{"derivedFrom":[makeQuery(id+"F3.boolean.opBoolean","MERGE",FACE,{"derivedFrom":[makeQuery(id+"F1.opExtrude","SWEPT_FACE",FACE,{"disambiguationData":[OSD([subQ1]),TDD([makeQuery(id+"F0.imprint","IMPRINT",EDGE,{"disambiguationData":[TD([[makeQuery(id+"F0.imprint","INTERSECT",VERTEX,{"derivedFrom":[sQuery(id+"F0.wireOp",EDGE,"E0.bottom"),subQ1]}),-1.0]])],"derivedFrom":subQ1})])]}),makeQuery(id+"F3.opExtrude","SWEPT_FACE",FACE,{"disambiguationData":[OSD([subQ0])]})]}),makeQuery(id+"F5.opExtrude","SWEPT_FACE",FACE,{"disambiguationData":[OSD([sQuery(id+"F4.wireOp",EDGE,"E18.right")])]})]})]});}
            var Q11;
            Q11=makeQuery(id+"F3.opExtrude","SWEPT_EDGE",EDGE,{"disambiguationData":[OSD([sQuery(id+"F0.wireOp",EDGE,"E4.top"),sQuery(id+"F0.wireOp",EDGE,"E4.right"),sQuery(id+"F0.wireOp",EDGE,"E5.right")])]});
            var Q12;
            Q12=makeQuery(id+"F9.opExtrude","SWEPT_EDGE",EDGE,{"disambiguationData":[OSD([sQuery(id+"F0.wireOp",EDGE,"E1.top"),sQuery(id+"F0.wireOp",EDGE,"E1.left"),sQuery(id+"F0.wireOp",EDGE,"E3.bottom"),sQuery(id+"F8.wireOp",EDGE,"E20.top"),sQuery(id+"F8.wireOp",EDGE,"E20.right")])]});
            var Q13;
            Q13=makeQuery(id+"F9.opExtrude","SWEPT_EDGE",EDGE,{"disambiguationData":[OSD([sQuery(id+"F0.wireOp",EDGE,"E1.bottom"),sQuery(id+"F0.wireOp",EDGE,"E1.left"),sQuery(id+"F0.wireOp",EDGE,"E3.top"),sQuery(id+"F8.wireOp",EDGE,"E20.top"),sQuery(id+"F8.wireOp",EDGE,"E20.left")])]});
            var Q14;
            Q14=makeQuery(id+"F7.opExtrude","SWEPT_EDGE",EDGE,{"disambiguationData":[OSD([sQuery(id+"F0.wireOp",EDGE,"E1.bottom"),sQuery(id+"F0.wireOp",EDGE,"E1.right"),sQuery(id+"F0.wireOp",EDGE,"E2.top"),sQuery(id+"F6.wireOp",EDGE,"E19.top"),sQuery(id+"F6.wireOp",EDGE,"E19.right")])]});
            var Q15;
            Q15=makeQuery(id+"F5.opExtrude","SWEPT_EDGE",EDGE,{"disambiguationData":[OSD([sQuery(id+"F0.wireOp",EDGE,"E4.top"),sQuery(id+"F0.wireOp",EDGE,"E4.left"),sQuery(id+"F0.wireOp",EDGE,"E5.left"),sQuery(id+"F4.wireOp",EDGE,"E18.top"),sQuery(id+"F4.wireOp",EDGE,"E18.left")])]});
            var Q16;
            Q16=makeQuery(id+"F5.opExtrude","SWEPT_EDGE",EDGE,{"disambiguationData":[OSD([sQuery(id+"F0.wireOp",EDGE,"E4.top"),sQuery(id+"F0.wireOp",EDGE,"E4.right"),sQuery(id+"F0.wireOp",EDGE,"E5.right"),sQuery(id+"F4.wireOp",EDGE,"E18.top"),sQuery(id+"F4.wireOp",EDGE,"E18.right")])]});
            var Q17;
            Q17=makeQuery(id+"F7.opExtrude","SWEPT_EDGE",EDGE,{"disambiguationData":[OSD([sQuery(id+"F0.wireOp",EDGE,"E1.top"),sQuery(id+"F0.wireOp",EDGE,"E1.right"),sQuery(id+"F0.wireOp",EDGE,"E2.bottom"),sQuery(id+"F6.wireOp",EDGE,"E19.top"),sQuery(id+"F6.wireOp",EDGE,"E19.left")])]});
            fillet(context, id + "F12", {"entities" : qUnion([Q0, Q1, Q2, Q3, Q4, Q5, Q6, Q7, Q8, Q9, Q10, Q11, Q12, Q13, Q14, Q15, Q16, Q17]), "radius" : 2 * mm, "tangentPropagation" : true, "allowEdgeOverflow" : false});
        }
        {
            var Q0;
            Q0=makeQuery(id+"F1.opExtrude","SWEPT_EDGE",EDGE,{"disambiguationData":[OSD([sQuery(id+"F0.wireOp",EDGE,"E0.top"),sQuery(id+"F0.wireOp",EDGE,"E0.right")])]});
            var Q1;
            Q1=makeQuery(id+"F1.opExtrude","SWEPT_EDGE",EDGE,{"disambiguationData":[OSD([sQuery(id+"F0.wireOp",EDGE,"E0.top"),sQuery(id+"F0.wireOp",EDGE,"E0.left")])]});
            var Q2;
            Q2=makeQuery(id+"F1.opExtrude","SWEPT_EDGE",EDGE,{"disambiguationData":[OSD([sQuery(id+"F0.wireOp",EDGE,"E0.bottom"),sQuery(id+"F0.wireOp",EDGE,"E0.left")])]});
            var Q3;
            Q3=makeQuery(id+"F1.opExtrude","SWEPT_EDGE",EDGE,{"disambiguationData":[OSD([sQuery(id+"F0.wireOp",EDGE,"E0.bottom"),sQuery(id+"F0.wireOp",EDGE,"E0.right")])]});
            fillet(context, id + "F13", {"entities" : qUnion([Q0, Q1, Q2, Q3]), "radius" : 9 * mm, "tangentPropagation" : true, "allowEdgeOverflow" : false});
        }
    });
